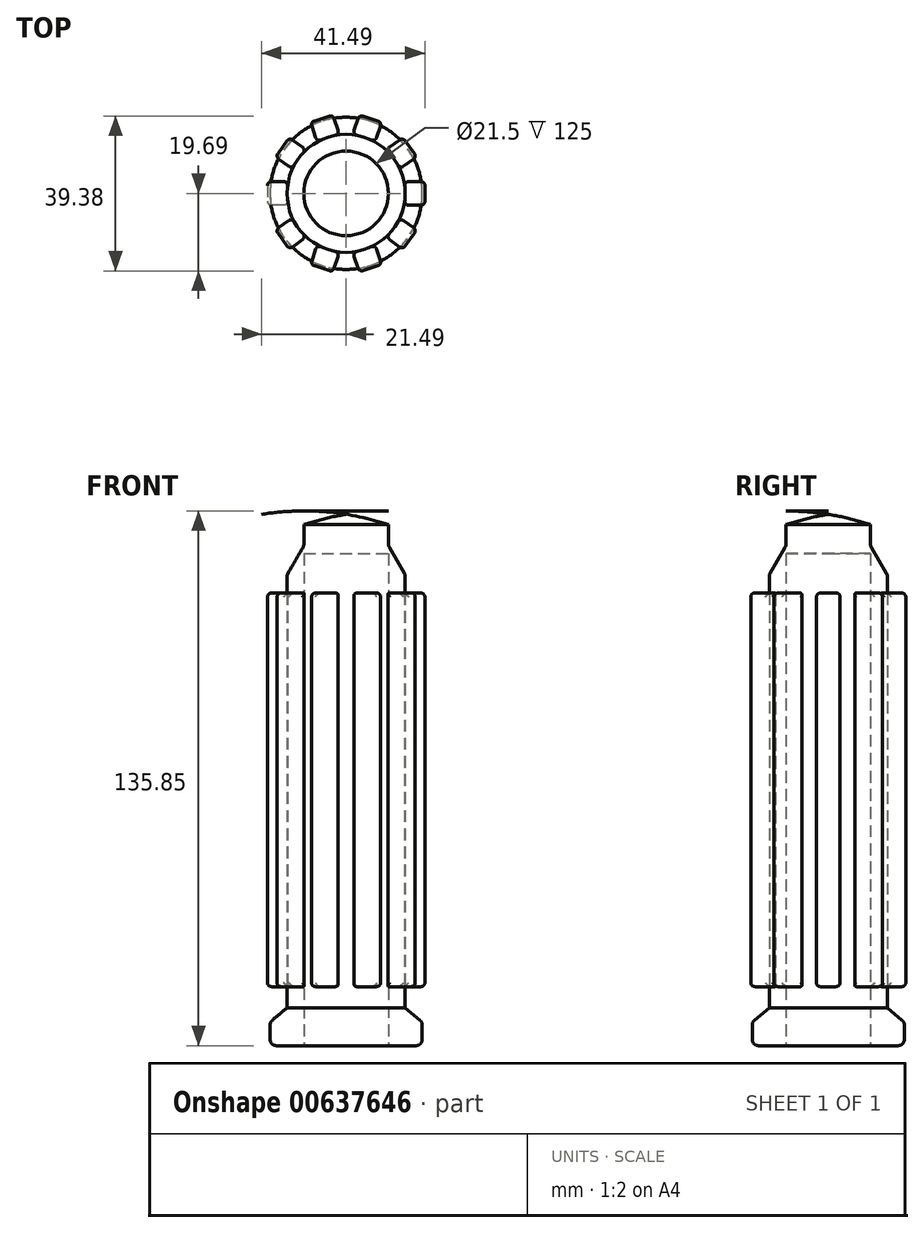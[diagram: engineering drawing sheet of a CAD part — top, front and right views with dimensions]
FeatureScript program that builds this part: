
annotation { "Feature Type Name" : "Feature", "Feature Type Description" : "" }
export const myFeature = defineFeature(function(context is Context, id is Id, definition is map)
    precondition{}
    {
        {
            var Q0;
            Q0=qCreatedBy(makeId("Front.planeOp"),FACE);
            var sketch = newSketch(context, id + "F0", { "sketchPlane" : qUnion([Q0])});
            skLineSegment(sketch, "E0", {"start": v(10.75, 0) * mm, "end": v(19.33, 0) * mm});
            skLineSegment(sketch, "E1", {"start": v(19.33, 0) * mm, "end": v(19.33, 6) * mm});
            skLineSegment(sketch, "E2", {"start": v(19.33, 6) * mm, "end": v(15, 9.63) * mm});
            skLineSegment(sketch, "E3", {"start": v(15, 9.63) * mm, "end": v(15, 119.63) * mm});
            skLineSegment(sketch, "E4", {"start": v(15, 119.63) * mm, "end": v(10.74, 127) * mm});
            skLineSegment(sketch, "E5", {"start": v(10.74, 127) * mm, "end": v(10.74, 132.37) * mm});
            skArc(sketch, "E6", {"start": v(10.74, 132.37) * mm, "mid": v(5.43, 133.9) * mm, "end": v(0, 135) * mm});
            skLineSegment(sketch, "E7", {"start": v(0, 135) * mm, "end": v(0, 125) * mm});
            skLineSegment(sketch, "E8", {"start": v(0, 125) * mm, "end": v(10.75, 125) * mm});
            skLineSegment(sketch, "E9", {"start": v(10.75, 125) * mm, "end": v(10.75, 0) * mm});
            skLineSegment(sketch, "E10", {"start": v(0, 0) * mm, "end": v(0, 53.71) * mm, "construction": true});
            skLineSegment(sketch, "E11", {"start": v(0, 53.71) * mm, "end": v(0, 125) * mm, "construction": true});
            skSolve(sketch);
        }
        {
            var Q0;
            Q0 = qSketchRegion(id + "F0", true);
            var Q1;
            Q1=sQuery(id+"F0.wireOp",EDGE,"E11");
            revolve(context, id + "F1", {"surfaceOperationType" : NewSurfaceOperationType.NEW, "entities" : qUnion([Q0]), "axis" : qUnion([Q1]), "revolveType" : RevolveType.FULL});
        }
        {
            var Q0;
            Q0=makeQuery(id+"F1.opRevolve","SWEPT_FACE",FACE,{"disambiguationData":[OSD([sQuery(id+"F0.wireOp",EDGE,"E4")])]});
            var Q1;
            Q1=makeQuery(id+"F1.opRevolve","SWEPT_FACE",FACE,{"disambiguationData":[OSD([sQuery(id+"F0.wireOp",EDGE,"E1")])]});
            fillet(context, id + "F2", {"entities" : qUnion([Q0, Q1]), "radius" : 1.6 * mm, "tangentPropagation" : true, "allowEdgeOverflow" : false});
        }
        {
            var Q0;
            Q0=qCreatedBy(makeId("Right.planeOp"),FACE);
            cPlane(context, id + "F3", {"entities" : qUnion([Q0]), "cplaneType" : CPlaneType.OFFSET, "offset" : 20 * mm, "width" : 150 * mm, "height" : 150 * mm});
        }
        {
            var Q0;
            Q0=qCreatedBy(id+"F3.planeOp",FACE);
            var sketch = newSketch(context, id + "F4", { "sketchPlane" : qUnion([Q0])});
            skLineSegment(sketch, "E12.bottom", {"start": v(-3, 115) * mm, "end": v(3, 115) * mm});
            skLineSegment(sketch, "E12.top", {"start": v(-3, 15) * mm, "end": v(3, 15) * mm});
            skLineSegment(sketch, "E12.left", {"start": v(-3, 115) * mm, "end": v(-3, 15) * mm});
            skLineSegment(sketch, "E12.right", {"start": v(3, 115) * mm, "end": v(3, 15) * mm});
            skSolve(sketch);
        }
        {
            var Q0;
            Q0 = qSketchRegion(id + "F4", true);
            var Q1;
            Q1=makeQuery(id+"F1.opRevolve","SWEPT_FACE",FACE,{"disambiguationData":[OSD([sQuery(id+"F0.wireOp",EDGE,"E3")])]});
            extrude(context, id + "F5", {"entities" : qUnion([Q0]), "endBound" : BoundingType.UP_TO_SURFACE, "oppositeDirection" : true, "depth" : 9.2 * mm, "endBoundEntityFace" : qUnion([Q1]), "offsetDistance" : 25 * mm});
        }
        {
            var Q0;
            Q0=makeQuery(id+"F5.opExtrude","CAP_EDGE",EDGE,{"disambiguationData":[OSD([sQuery(id+"F4.wireOp",EDGE,"E12.left")])],"isStart":true});
            var Q1;
            Q1=makeQuery(id+"F5.opExtrude","CAP_EDGE",EDGE,{"disambiguationData":[OSD([sQuery(id+"F4.wireOp",EDGE,"E12.right")])],"isStart":true});
            var Q2;
            Q2=makeQuery(id+"F5.opExtrude","CAP_EDGE",EDGE,{"disambiguationData":[OSD([sQuery(id+"F4.wireOp",EDGE,"E12.left")])],"isStart":false});
            var Q3;
            Q3=makeQuery(id+"F5.opExtrude","CAP_EDGE",EDGE,{"disambiguationData":[OSD([sQuery(id+"F4.wireOp",EDGE,"E12.right")])],"isStart":false});
            var Q4;
            Q4=makeQuery(id+"F5.opExtrude","CAP_EDGE",EDGE,{"disambiguationData":[OSD([sQuery(id+"F4.wireOp",EDGE,"E12.bottom")])],"isStart":true});
            var Q5;
            Q5=makeQuery(id+"F5.opExtrude","SWEPT_EDGE",EDGE,{"disambiguationData":[OSD([sQuery(id+"F4.wireOp",EDGE,"E12.bottom"),sQuery(id+"F4.wireOp",EDGE,"E12.right")])]});
            var Q6;
            Q6=makeQuery(id+"F5.opExtrude","SWEPT_EDGE",EDGE,{"disambiguationData":[OSD([sQuery(id+"F4.wireOp",EDGE,"E12.bottom"),sQuery(id+"F4.wireOp",EDGE,"E12.left")])]});
            var Q7;
            Q7=makeQuery(id+"F5.opExtrude","CAP_EDGE",EDGE,{"disambiguationData":[OSD([sQuery(id+"F4.wireOp",EDGE,"E12.top")])],"isStart":true});
            var Q8;
            Q8=makeQuery(id+"F5.opExtrude","SWEPT_EDGE",EDGE,{"disambiguationData":[OSD([sQuery(id+"F4.wireOp",EDGE,"E12.top"),sQuery(id+"F4.wireOp",EDGE,"E12.right")])]});
            var Q9;
            Q9=makeQuery(id+"F5.opExtrude","SWEPT_EDGE",EDGE,{"disambiguationData":[OSD([sQuery(id+"F4.wireOp",EDGE,"E12.top"),sQuery(id+"F4.wireOp",EDGE,"E12.left")])]});
            fillet(context, id + "F6", {"entities" : qUnion([Q0, Q1, Q2, Q3, Q4, Q5, Q6, Q7, Q8, Q9]), "radius" : 1 * mm, "tangentPropagation" : true, "allowEdgeOverflow" : false});
        }
        {
            var Q0;
            Q0=makeQuery(id+"F5.opExtrude","SWEPT_BODY",BODY,{"disambiguationData":[OSD([sQuery(id+"F4.wireOp",EDGE,"E12.bottom"),sQuery(id+"F4.wireOp",EDGE,"E12.top"),sQuery(id+"F4.wireOp",EDGE,"E12.left"),sQuery(id+"F4.wireOp",EDGE,"E12.right")])]});
            var Q1;
            Q1=makeQuery(id+"F1.opRevolve","SWEPT_FACE",FACE,{"disambiguationData":[OSD([sQuery(id+"F0.wireOp",EDGE,"E3")])]});
            circularPattern(context, id + "F7", {"entities" : qUnion([Q0]), "axis" : qUnion([Q1]), "angle" : 360 * degree, "instanceCount" : 10, "equalSpace" : true});
        }
    });
